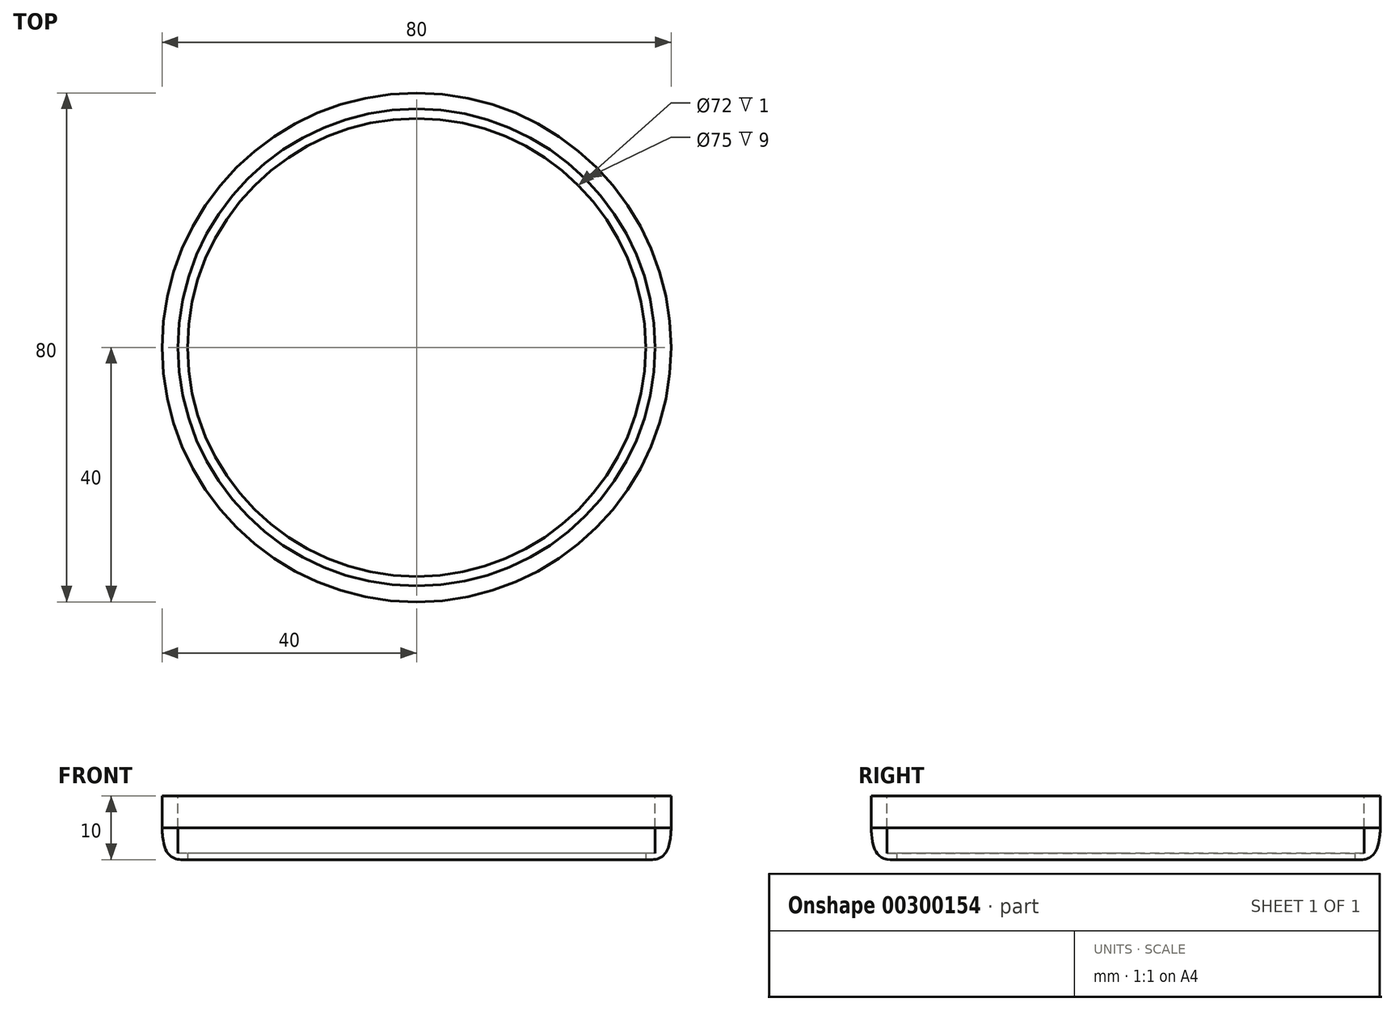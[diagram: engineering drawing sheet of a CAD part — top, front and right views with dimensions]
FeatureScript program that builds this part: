
annotation { "Feature Type Name" : "Feature", "Feature Type Description" : "" }
export const myFeature = defineFeature(function(context is Context, id is Id, definition is map)
    precondition{}
    {
        {
            var Q0;
            Q0=qCreatedBy(makeId("Front.planeOp"),FACE);
            var sketch = newSketch(context, id + "F0", { "sketchPlane" : qUnion([Q0])});
            skLineSegment(sketch, "E0", {"start": v(0, 0) * mm, "end": v(0, 28.2) * mm, "construction": true});
            skLineSegment(sketch, "E1", {"start": v(36, 0) * mm, "end": v(37, 0) * mm});
            skLineSegment(sketch, "E2", {"start": v(36, 10) * mm, "end": v(40, 10) * mm});
            skLineSegment(sketch, "E3", {"start": v(40, 10) * mm, "end": v(40, 5) * mm});
            skLineSegment(sketch, "E4", {"start": v(40, 5) * mm, "end": v(0, 5) * mm, "construction": true});
            skFitSpline(sketch, "E5", {"points": [v(37, 0) * mm, v(39.46, 1.63) * mm, v(40, 5) * mm], "startDerivative": vector(6.93, 0) * mm, "endDerivative": vector(0, 1.96) * mm});
            skPoint(sketch, "E6.orphan", {"position": v(40, 0) * mm});
            skLineSegment(sketch, "E7", {"start": v(36, 0) * mm, "end": v(36, 10) * mm});
            skSolve(sketch);
        }
        {
            var Q0;
            Q0 = qSketchRegion(id + "F0", true);
            var Q1;
            Q1=sQuery(id+"F0.wireOp",EDGE,"E0");
            revolve(context, id + "F1", {"entities" : qUnion([Q0]), "axis" : qUnion([Q1]), "revolveType" : RevolveType.FULL});
        }
        {
            var Q0;
            Q0=makeQuery(id+"F1.opRevolve","SWEPT_FACE",FACE,{"disambiguationData":[OSD([sQuery(id+"F0.wireOp",EDGE,"E2")])]});
            var sketch = newSketch(context, id + "F2", { "sketchPlane" : qUnion([Q0])});
            skCircle(sketch, "E8", {"center": v(0, 0) * mm, "radius": 37.5 * mm});
            skSolve(sketch);
        }
        {
            var Q0;
            Q0 = qSketchRegion(id + "F2", true);
            extrude(context, id + "F3", {"entities" : qUnion([Q0]), "operationType" : NewBodyOperationType.REMOVE, "oppositeDirection" : true, "depth" : 9 * mm});
        }
    });
